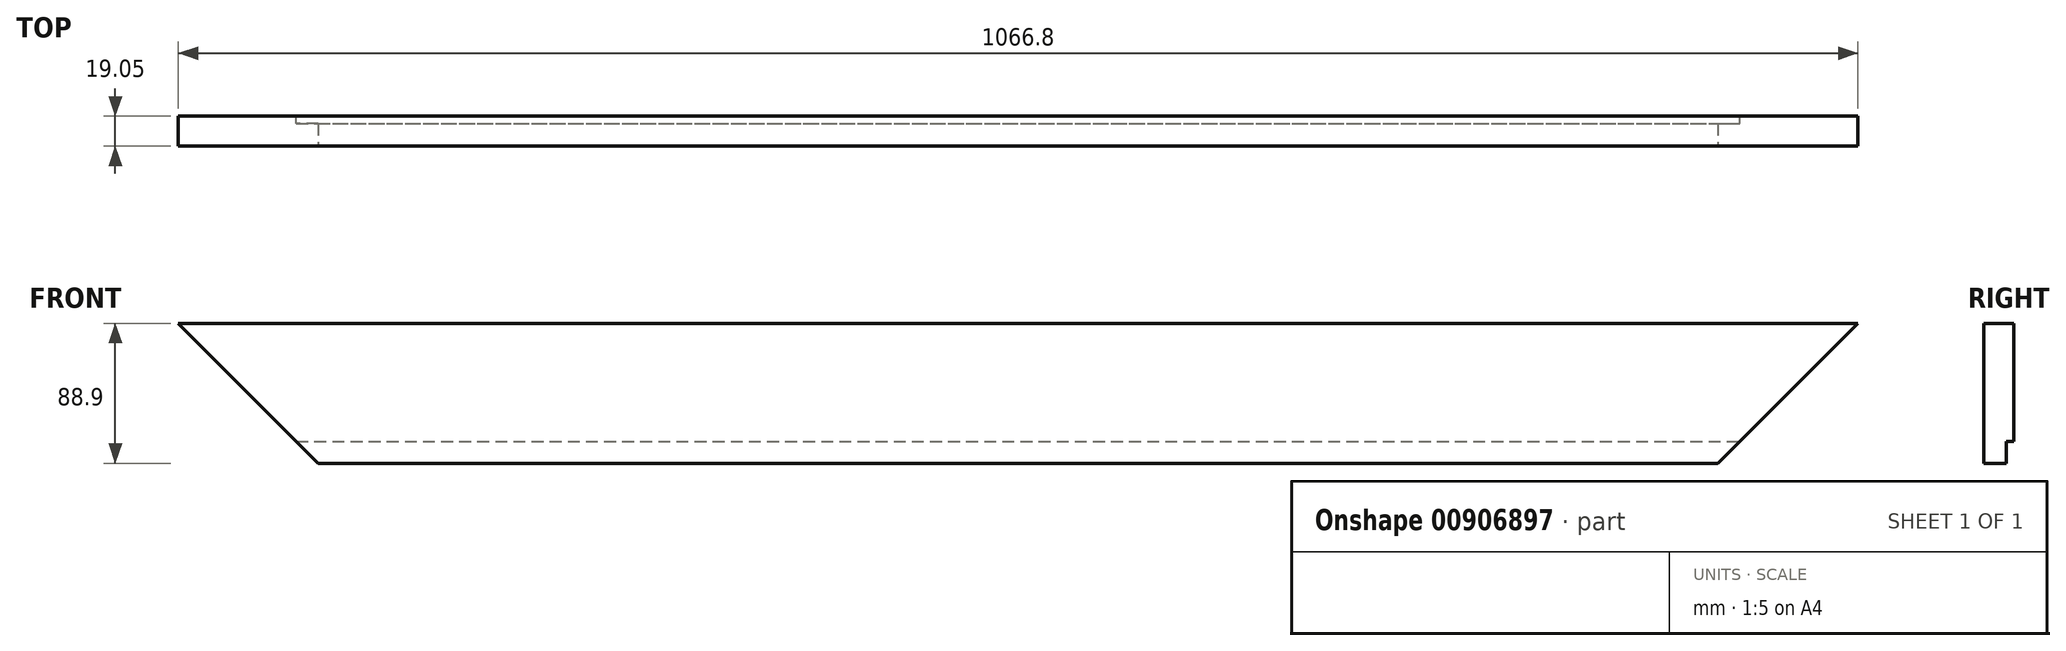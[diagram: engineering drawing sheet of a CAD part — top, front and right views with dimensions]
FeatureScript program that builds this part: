
annotation { "Feature Type Name" : "Feature", "Feature Type Description" : "" }
export const myFeature = defineFeature(function(context is Context, id is Id, definition is map)
    precondition{}
    {
        {
            var Q0;
            Q0=qCreatedBy(makeId("Front.planeOp"),FACE);
            var sketch = newSketch(context, id + "F0", { "sketchPlane" : qUnion([Q0])});
            skLineSegment(sketch, "E0.bottom", {"start": v(-533.4, 0) * mm, "end": v(533.4, 0) * mm});
            skLineSegment(sketch, "E0.top", {"start": v(-533.4, 88.9) * mm, "end": v(533.4, 88.9) * mm});
            skLineSegment(sketch, "E0.left", {"start": v(-533.4, 0) * mm, "end": v(-533.4, 88.9) * mm});
            skLineSegment(sketch, "E0.right", {"start": v(533.4, 0) * mm, "end": v(533.4, 88.9) * mm});
            skSolve(sketch);
        }
        {
            var Q0;
            Q0 = qSketchRegion(id + "F0", true);
            extrude(context, id + "F1", {"entities" : qUnion([Q0]), "depth" : 19.05 * mm, "offsetDistance" : 25.4 * mm});
        }
        {
            var Q0;
            Q0=makeQuery(id+"F1.opExtrude","SWEPT_FACE",FACE,{"disambiguationData":[OSD([sQuery(id+"F0.wireOp",EDGE,"E0.right")])]});
            var sketch = newSketch(context, id + "F2", { "sketchPlane" : qUnion([Q0])});
            skLineSegment(sketch, "E1", {"start": v(0, 0) * mm, "end": v(-4.76, 0) * mm});
            skLineSegment(sketch, "E2", {"start": v(-4.76, 0) * mm, "end": v(-4.76, 13.97) * mm});
            skPoint(sketch, "E2.endSnap0", {"position": v(-19.05, 44.45) * mm});
            skLineSegment(sketch, "E3", {"start": v(-4.76, 13.97) * mm, "end": v(0, 13.97) * mm});
            skLineSegment(sketch, "E4", {"start": v(0, 13.97) * mm, "end": v(0, 0) * mm});
            skSolve(sketch);
        }
        {
            var Q0;
            Q0 = qSketchRegion(id + "F2", true);
            extrude(context, id + "F3", {"entities" : qUnion([Q0]), "operationType" : NewBodyOperationType.REMOVE, "endBound" : BoundingType.THROUGH_ALL, "oppositeDirection" : true, "depth" : 25.4 * mm, "offsetDistance" : 25.4 * mm});
        }
        {
            var Q0;
            Q0=makeQuery(id+"F1.opExtrude","CAP_FACE",FACE,{"disambiguationData":[OSD([sQuery(id+"F0.wireOp",EDGE,"E0.bottom"),sQuery(id+"F0.wireOp",EDGE,"E0.top"),sQuery(id+"F0.wireOp",EDGE,"E0.left"),sQuery(id+"F0.wireOp",EDGE,"E0.right")])],"isStart":false});
            var sketch = newSketch(context, id + "F4", { "sketchPlane" : qUnion([Q0])});
            skLineSegment(sketch, "E5", {"start": v(-533.4, 88.9) * mm, "end": v(-444.5, 0) * mm});
            skLineSegment(sketch, "E6", {"start": v(-444.5, 0) * mm, "end": v(-533.4, 0) * mm});
            skLineSegment(sketch, "E7", {"start": v(-533.4, 0) * mm, "end": v(-533.4, 88.9) * mm});
            skLineSegment(sketch, "E8", {"start": v(0, 0) * mm, "end": v(0, 384.02) * mm, "construction": true});
            skLineSegment(sketch, "E9.MirrorCS", {"start": v(533.4, 0) * mm, "end": v(533.4, 88.9) * mm});
            skLineSegment(sketch, "E10.MirrorCS", {"start": v(533.4, 88.9) * mm, "end": v(444.5, 0) * mm});
            skLineSegment(sketch, "E11.MirrorCS", {"start": v(444.5, 0) * mm, "end": v(533.4, 0) * mm});
            skSolve(sketch);
        }
        {
            var Q0;
            Q0 = qSketchRegion(id + "F4", true);
            extrude(context, id + "F5", {"entities" : qUnion([Q0]), "operationType" : NewBodyOperationType.REMOVE, "endBound" : BoundingType.THROUGH_ALL, "oppositeDirection" : true, "depth" : 25.4 * mm, "offsetDistance" : 25.4 * mm});
        }
    });
